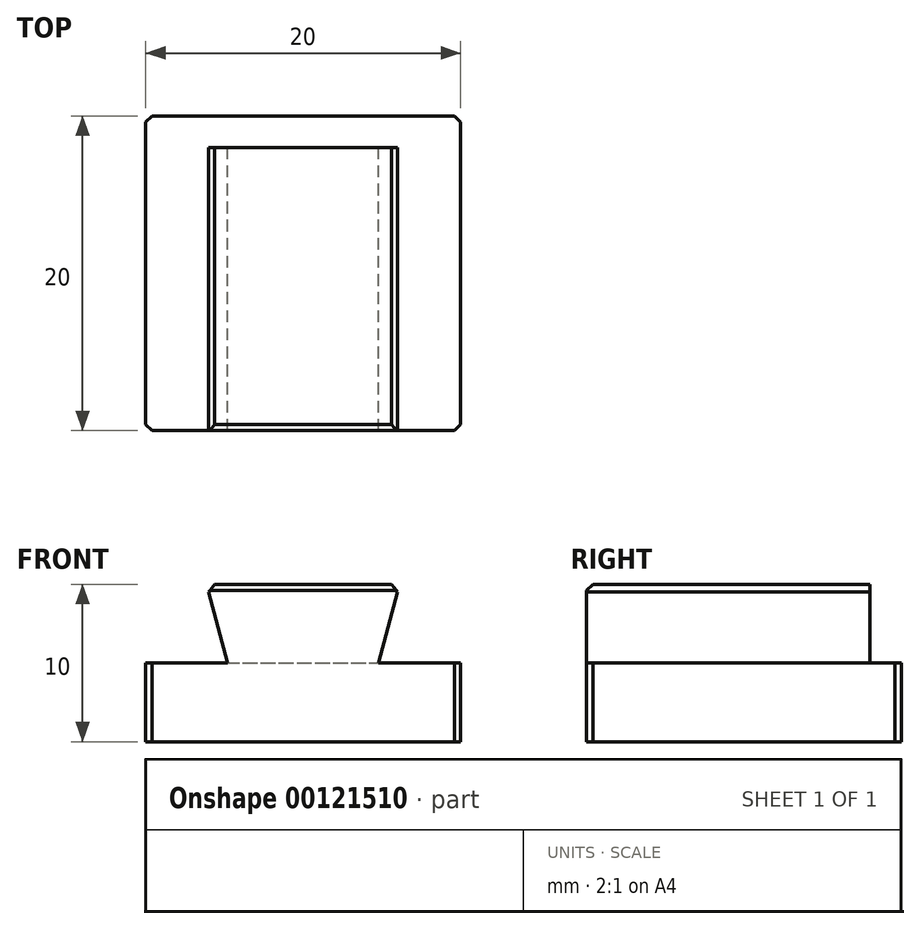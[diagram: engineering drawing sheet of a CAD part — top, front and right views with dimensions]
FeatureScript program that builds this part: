
annotation { "Feature Type Name" : "Feature", "Feature Type Description" : "" }
export const myFeature = defineFeature(function(context is Context, id is Id, definition is map)
    precondition{}
    {
        {
            assignVariable(context, id + "F0", {"name" : "PrintOffset", "anyValue" : 0.4});
        }
        {
            assignVariable(context, id + "F1", {"name" : "DovetailBackstopDepth", "anyValue" : 2});
        }
        {
            assignVariable(context, id + "F2", {"name" : "DovetailDepth", "anyValue" : 20});
        }
        {
            var Q0;
            Q0=qCreatedBy(makeId("Front.planeOp"),FACE);
            var sketch = newSketch(context, id + "F3", { "sketchPlane" : qUnion([Q0])});
            skLineSegment(sketch, "E0", {"start": v(-10, 0) * mm, "end": v(10, 0) * mm});
            skLineSegment(sketch, "E1", {"start": v(-10, 0) * mm, "end": v(-10, 10) * mm});
            skLineSegment(sketch, "E2", {"start": v(10, 10) * mm, "end": v(10, 0) * mm});
            skLineSegment(sketch, "E3", {"start": v(-10, 5) * mm, "end": v(10, 5) * mm});
            skLineSegment(sketch, "E4", {"start": v(-10, 10) * mm, "end": v(10, 10) * mm});
            skLineSegment(sketch, "E5", {"start": v(-6.14, 10) * mm, "end": v(-4.8, 5) * mm});
            skLineSegment(sketch, "E6", {"start": v(0, 0) * mm, "end": v(0, 10) * mm, "construction": true});
            skLineSegment(sketch, "E7.MirrorCS", {"start": v(6.14, 10) * mm, "end": v(4.8, 5) * mm});
            skSolve(sketch);
        }
        {
            var Q0;
            Q0=makeQuery(id+"F3.imprint","IMPRINT",FACE,{"disambiguationData":[TD([[makeQuery(id+"F3.imprint","IMPRINT",EDGE,{"derivedFrom":sQuery(id+"F3.wireOp",EDGE,"E0")}),1.0]])]});
            var Q1;
            {var subQ0=sQuery(id+"F3.wireOp",EDGE,"E5");Q1=makeQuery(id+"F3.imprint","IMPRINT",FACE,{"disambiguationData":[TD([[makeQuery(id+"F3.imprint","IMPRINT",EDGE,{"derivedFrom":subQ0}),1.0]])]});}
            extrude(context, id + "F4", {"entities" : qUnion([Q0, Q1]), "depth" : (getVariable(context, 'DovetailDepth')) * mm});
        }
        {
            var Q0;
            {var subQ0=sQuery(id+"F3.wireOp",EDGE,"E5");Q0=makeQuery(id+"F3.imprint","IMPRINT",FACE,{"disambiguationData":[TD([[makeQuery(id+"F3.imprint","IMPRINT",EDGE,{"derivedFrom":subQ0}),1.0]])]});}
            extrude(context, id + "F5", {"entities" : qUnion([Q0]), "operationType" : NewBodyOperationType.REMOVE, "depth" : (getVariable(context, 'DovetailBackstopDepth')) * mm});
        }
        {
            var Q0;
            Q0=makeQuery(id+"F4.opExtrude","SWEPT_EDGE",EDGE,{"disambiguationData":[OSD([sQuery(id+"F3.wireOp",EDGE,"E4"),sQuery(id+"F3.wireOp",EDGE,"E7.MirrorCS")])]});
            var Q1;
            Q1=makeQuery(id+"F4.opExtrude","SWEPT_EDGE",EDGE,{"disambiguationData":[OSD([sQuery(id+"F3.wireOp",EDGE,"E4"),sQuery(id+"F3.wireOp",EDGE,"E5")])]});
            var Q2;
            Q2=makeQuery(id+"F4.opExtrude","CAP_EDGE",EDGE,{"disambiguationData":[OSD([sQuery(id+"F3.wireOp",EDGE,"E4")])],"isStart":false});
            var Q3;
            Q3=makeQuery(id+"F5.boolean.opBoolean","COPY",EDGE,{"derivedFrom":makeQuery(id+"F5.opExtrude","CAP_EDGE",EDGE,{"disambiguationData":[OSD([sQuery(id+"F3.wireOp",EDGE,"E4")])],"isStart":false})});
            var Q4;
            Q4=makeQuery(id+"F4.opExtrude","CAP_EDGE",EDGE,{"disambiguationData":[OSD([sQuery(id+"F3.wireOp",EDGE,"E2")])],"isStart":false});
            var Q5;
            Q5=makeQuery(id+"F4.opExtrude","CAP_EDGE",EDGE,{"disambiguationData":[OSD([sQuery(id+"F3.wireOp",EDGE,"E2")])],"isStart":true});
            var Q6;
            Q6=makeQuery(id+"F4.opExtrude","CAP_EDGE",EDGE,{"disambiguationData":[OSD([sQuery(id+"F3.wireOp",EDGE,"E1")])],"isStart":false});
            var Q7;
            Q7=makeQuery(id+"F4.opExtrude","CAP_EDGE",EDGE,{"disambiguationData":[OSD([sQuery(id+"F3.wireOp",EDGE,"E1")])],"isStart":true});
            chamfer(context, id + "F6", {"entities" : qUnion([Q0, Q1, Q2, Q3, Q4, Q5, Q6, Q7]), "width" : (getVariable(context, 'PrintOffset')) * mm, "tangentPropagation" : true});
        }
    });
